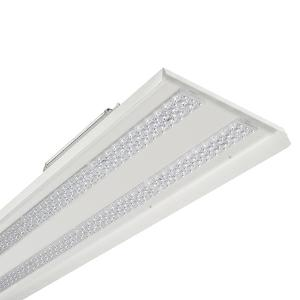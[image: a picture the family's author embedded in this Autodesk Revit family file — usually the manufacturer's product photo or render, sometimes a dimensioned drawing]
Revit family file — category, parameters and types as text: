
# Revit family: 3f_filippi_-_kit_led_retrofit_beta_430_2x_3f_filippi_-_a5308_a5322_-_kit_led_beta_430_-_l1551-_2x65w_ampio___vs_75b5
name_source: partatom
category: Lighting Fixtures
units: mm (PartAtom-declared; Revit-internal decimal feet)

## family parameters
Cut with Voids When Loaded = No
Host = Face
Light Source = No
Part Type = Normal
Room Calculation Point = No
Round Connector Dimension = Use Diameter
Shared = No

## types (1)
- 3F Filippi - Kit LED Retrofit Beta 430 2X (1 x LED, 17494 lm, 120 W, 4000 K)
    Apparent Load = 120 VA
    Approval mark = ENEC
    CIE Flux Codes = 67 92 98 100 100
    Color Rendering = 80
    Color Temperature = 4000 K
    Control Gear = Electronic ballast
    Default Elevation = 1800 mm
    Description = Beta 430 Retrofit Kit to replace the 4x49W T5 Amalgam or the 4x58W T8 version

ILLUMINOTECHNICAL
Luminous efficiency 100% (DLOR 100%, ULOR 0%).
Initial luminous flux of the luminaire 17494 lm.
Wide symmetric distribution.
Installation Interdistance Transv.D = 1.34 x hu - Long.D = 1.34 x hu.
Tabular UGR (CIE 117 - 4H-8H; S=0.25H; 70/50/20): RUG 19.5 - 20.
Beam angle: 88° - 88°.
Luminous efficacy 146 lm/W.
Lifetime (L93/B10): 30000 h. (tq+25°C)
Lifetime (L90/B10): 50000 h. (tq+25°C)
Lifetime (L85/B10): 80000 h. (tq+25°C)
Lifetime (L80/B10): 100000 h. (tq+25°C)
Lifetime (L85/B10): 50000 h. (tq+40°C)
Sudden decreased luminous flux after 50000 hours: 0% (C0).
Photobiological safety in compliance with IEC/TR 62778: RG0 risk exempt, (IEC 62471).
In compliance with IEC/EN 62722-2-1 - IEC/EN 62717 standards.

SOURCE
2 linear LED modules 65W/840.
Energy efficiency class (UE 2019/2020 - UE 2019/2015): C.
CIE 13.3 Colour rendering index: CRI >80 (R9 <50%).
IES TM-30 Fidelity Index: Rf = 84 Rg = 95.
CCT nominal colour temperature 4000 K.
Colour initial tolerance (MacAdam): SDCM 3.

MECHANICAL
Gear-tray unit hot-galvanised steel, painted in white polyester.
Methacrylate (PMMA) lenses with external flat surface.
Luminaire with limited surface temperature. - D - (EN 60598-2-24)
Dimensions: 1551x430 mm, height 159 mm. Weight 13.067 kg.
Mechanical strength to impacts IK08 (5 joule).
Glow-wire test resistance 850°C.

ELECTRICAL
Halogen Free electronic wiring 230V-50/60Hz, power factor 0.97, THD <25%, constant output current, class I, 2 driver.
Twin-circuit.
Power of the luminaire 120 W.
CE - IEC 60598-1 - EN 60598-1.
SAFE FLICKER: PstLM=<1 and SVM=<0.4 (IEC TR 61547-1 and IEC TR 63158), to ensure a more comfortable and safe light.
Luminaire compliant with EN 60598-2-22 for power supply from a centralised emergency system CPSS (Central Power Supply System), not incorporated in the luminaire - high risk areas excluded. The default power and flux are 100% in AC and 100% in DC.
Ambient temperature from -20°C to +40°C.
Temperature class T6 max 85°C.
Relative humidity UR: <85%.

INSTALLATION
Retrofit.
Correct installation of the retrofit LED kit, compliant with EN 60598-1 and CE marked, inside the 3F Filippi - Beta 4x and 6x i3F 76 Fluorescent luminaires must be only carried out by qualified personnel to ensure compliance with the national installation standards.
Attention: to maintain the degree of protection of the device and for the purposes of validity of the guarantee of the new retrofit kits, it is imperative to replace the old cable guides (on the body of the device) with the new ones supplied.
All accessories dedicated to this product are available on the Catalog and on our website www.3F-Filippi.com.

ACCESSORIES
A5322 - Printed glass with Beta 430 frame - L1551.

WARNING
Fixture not suitable for cold stores with an ambient temperature <0°C and/or relative humidity >85%.
Luminaire designed for disposal/recycling at end-of-life.
Replaceable (LED only) light source by a professional. Replaceable control gear by a professional.
    Height = 159 mm
    Lamp = 1 x LED
    Lamp Light Flux = 17494 lm
    Lamp Power = 120 W
    Lamp count = 1
    Length = 1551 mm
    Lifetime = 50000 h
    Luminous efficacy = 146 lm/W
    Manufacturer = 3F Filippi
    ModVariant = No
    Model = 3F Filippi - A5308+A5322 - Kit LED Beta 430 - L1551- 2X65W AMPIO + VS
    Mounting Place = Ceiling
    Mounting Type = Surface mounted
    Number of Poles = 1
    OnlyDefault = Yes
    Power Factor = 1
    Product Name = 3F Filippi - Kit LED Retrofit Beta 430 2X
    Product group = ceiling mounted luminaire
    ProductGroupID = 3
    Protection Class = Protection class I
    Protection Degree = Degree of protection
    RLX_Detail_Level = 1
    RLX_Emergency_Light_Flux = 0 lm
    RLX_Emergency_Type = 0
    RLX_Emergency_Type_DB = No
    RlxData = <blob elided: 70649 chars, md5=52998452>
    Socket = socket
    Standby Power = 0 W
    System Light Flux = 17494 lm
    System Power = 120 W
    Type Comments = Product without accessories
    Type Image = 3ffilippi_a5308_a5322.jpg
    URL = http://relux.com
    VarID = ---
    Voltage = 0 V
    Weight = 0.00 kg
    Width = 430 mm

## geometry (parser evidence)
native form markers: Blend x4, Sweep x10
no freeform markers — native parametric forms only
